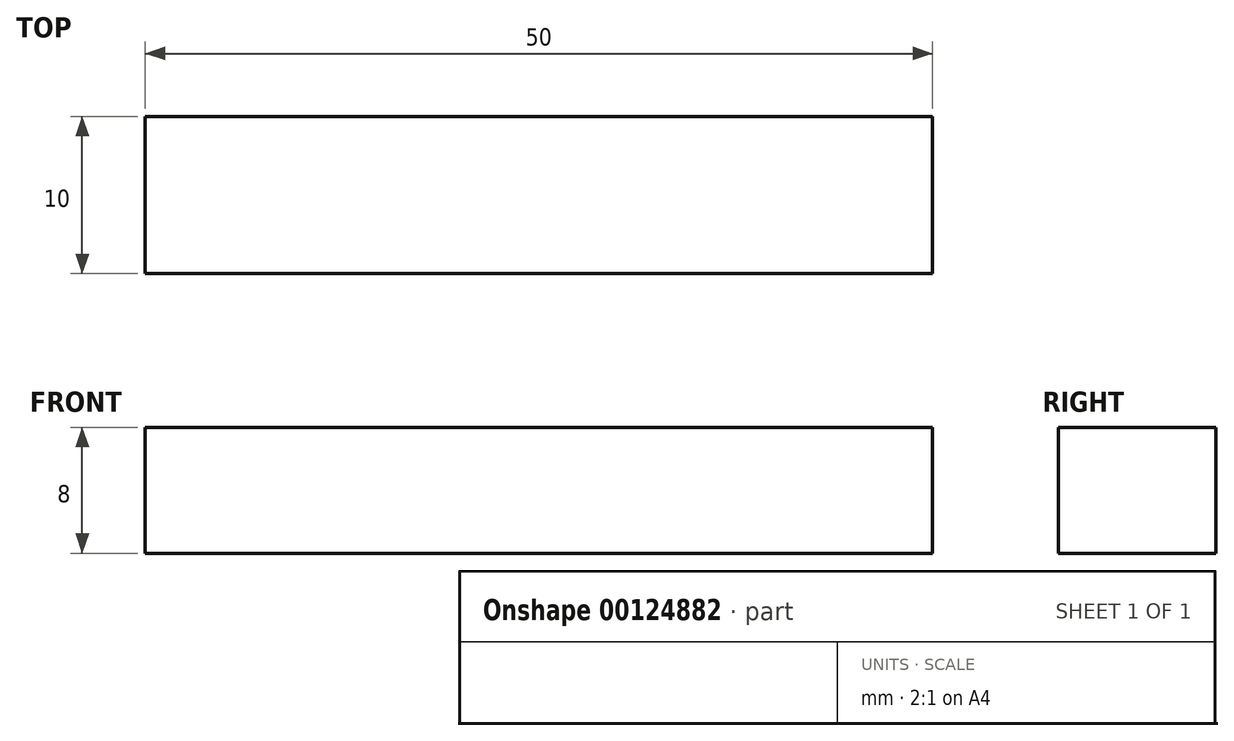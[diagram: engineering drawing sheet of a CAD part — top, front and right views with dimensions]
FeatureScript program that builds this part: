
annotation { "Feature Type Name" : "Feature", "Feature Type Description" : "" }
export const myFeature = defineFeature(function(context is Context, id is Id, definition is map)
    precondition{}
    {
        {
            var Q0;
            Q0=qCreatedBy(makeId("Right.planeOp"),FACE);
            var sketch = newSketch(context, id + "F0", { "sketchPlane" : qUnion([Q0])});
            skLineSegment(sketch, "E0.bottom", {"start": v(-5, 4) * mm, "end": v(5, 4) * mm});
            skLineSegment(sketch, "E0.top", {"start": v(-5, -4) * mm, "end": v(5, -4) * mm});
            skLineSegment(sketch, "E0.left", {"start": v(-5, 4) * mm, "end": v(-5, -4) * mm});
            skLineSegment(sketch, "E0.right", {"start": v(5, 4) * mm, "end": v(5, -4) * mm});
            skPoint(sketch, "E0.middle", {"position": v(0, 0) * mm});
            skSolve(sketch);
        }
        {
            var Q0;
            Q0=makeQuery(id+"F0.imprint","IMPRINT",FACE,{"disambiguationData":[TD([[makeQuery(id+"F0.imprint","IMPRINT",EDGE,{"derivedFrom":sQuery(id+"F0.wireOp",EDGE,"E0.bottom")}),-1.0]])]});
            extrude(context, id + "F1", {"entities" : qUnion([Q0]), "depth" : 50 * mm});
        }
    });
